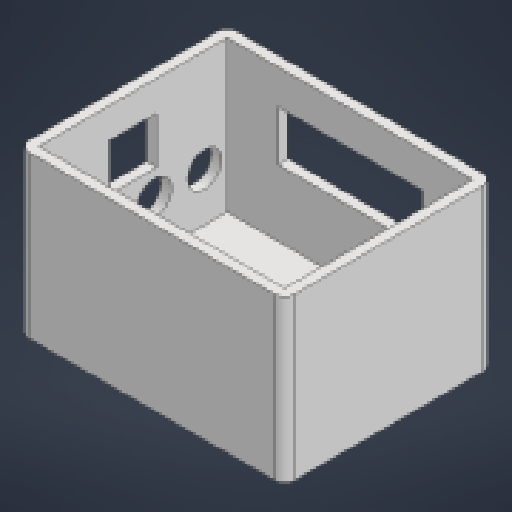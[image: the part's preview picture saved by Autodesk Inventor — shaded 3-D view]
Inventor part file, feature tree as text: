
AUTODESK INVENTOR PART (.ipt)
format: ipt  version: 2025.2 (Build 292293000, 293)  size: 204,800 bytes
history: native  units: mm
features: extrude x8, sketch x6, other x4, reference x3, fillet x1, mirror x1
ambient origin geometry x8: Origin, YZ Plane, XZ Plane, XY Plane, X Axis, Y Axis, Z Axis, Center Point
bodies: Solid1 (feature_tree)
feature tree (23):
  sketch  "Sketch1"  dims[d2=5.0mm d3=5.0mm d4=0.0mm]
  extrude  "Extrusion1"  Depth=5.0mm TaperAngle=0.0deg
  extrude  "Extrusion2"  Depth=75.0mm
  extrude  "Extrusion3"  Depth=1.0mm
  fillet  "Fillet1"  Radius=1.0mm
  extrude  "Extrusion4"  Depth=5.0mm
  extrude  "Extrusion5"  Depth=1.0mm
  mirror  "Mirror1"
  extrude  "Extrusion6"  Depth=1.0mm
  extrude  "Extrusion7"  Depth=4.0mm
  extrude  "Extrusion8"  Depth=20.0mm
  sketch  "Sketch2"  dims[d5=75.0mm d6=0.0mm d7=57.0mm]
  reference  "Reference1"
  reference  "Reference2"
  sketch  "Sketch3"  dims[d8=89.0mm d9=3.5mm d10=1.0mm]
  sketch  "Sketch4"  dims[d11=56.0mm d12=5.0mm]
  reference  "Reference5"
  sketch  "Sketch5"  dims[d13=3.0mm d14=1.0mm]
  sketch  "Sketch6"  dims[d15=81.0mm d16=1.0mm d17=4.0mm d18=20.0mm d19=10.0mm d20=0.0mm d21=5.0mm d24=75.0mm d25=0.0mm d26=29.0mm d27=23.0mm d28=23.2mm d29=15.0mm d30=10.0mm d31=0.0mm d32=72.0mm d33=25.0mm d34=17.0mm d35=10.0mm d36=0.0mm d37=60.0mm d38=20.0mm d39=41.0mm d40=12.0mm d41=10.0mm d42=0.0mm d43=12.0mm d44=7.0mm d45=12.0mm d46=6.0mm d47=10.0mm d48=0.0mm]
  other  "<userpath>\Desktop\Naks\Sklop.iam"
  other  "Sklop.iam"
  other  "ultrasonic:1"
  other  "display:1"
